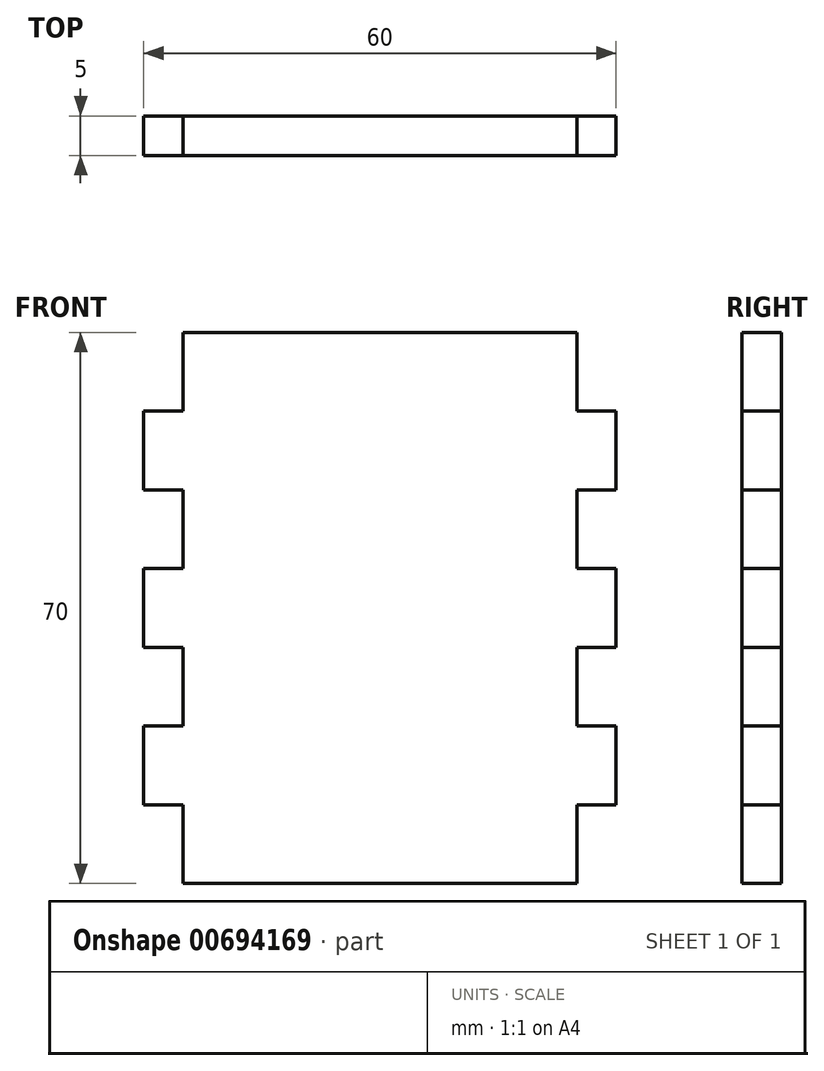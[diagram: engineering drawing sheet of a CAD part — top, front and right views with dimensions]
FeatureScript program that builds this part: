
annotation { "Feature Type Name" : "Feature", "Feature Type Description" : "" }
export const myFeature = defineFeature(function(context is Context, id is Id, definition is map)
    precondition{}
    {
        {
            var Q0;
            Q0=qCreatedBy(makeId("Front.planeOp"),FACE);
            var sketch = newSketch(context, id + "F0", { "sketchPlane" : qUnion([Q0])});
            skLineSegment(sketch, "E0.bottom", {"start": v(0, 70) * mm, "end": v(-25, 70) * mm});
            skLineSegment(sketch, "E0.top", {"start": v(0, 0) * mm, "end": v(-25, 0) * mm});
            skLineSegment(sketch, "E0.left", {"start": v(0, 70) * mm, "end": v(0, 0) * mm});
            skLineSegment(sketch, "E0.right", {"start": v(-30, 60) * mm, "end": v(-30, 50) * mm});
            skLineSegment(sketch, "E1.top", {"start": v(-30, 60) * mm, "end": v(-25, 60) * mm});
            skLineSegment(sketch, "E1.right", {"start": v(-25, 70) * mm, "end": v(-25, 60) * mm});
            skLineSegment(sketch, "E2.bottom", {"start": v(-30, 50) * mm, "end": v(-25, 50) * mm});
            skLineSegment(sketch, "E2.top", {"start": v(-30, 40) * mm, "end": v(-25, 40) * mm});
            skLineSegment(sketch, "E2.right", {"start": v(-25, 50) * mm, "end": v(-25, 40) * mm});
            skLineSegment(sketch, "E3.bottom", {"start": v(-30, 30) * mm, "end": v(-25, 30) * mm});
            skLineSegment(sketch, "E3.top", {"start": v(-30, 20) * mm, "end": v(-25, 20) * mm});
            skLineSegment(sketch, "E3.right", {"start": v(-25, 30) * mm, "end": v(-25, 20) * mm});
            skLineSegment(sketch, "E4.bottom", {"start": v(-30, 10) * mm, "end": v(-25, 10) * mm});
            skLineSegment(sketch, "E4.right", {"start": v(-25, 10) * mm, "end": v(-25, 0) * mm});
            skLineSegment(sketch, "E5.trimOffspring", {"start": v(-30, 40) * mm, "end": v(-30, 30) * mm});
            skLineSegment(sketch, "E6.trimOffspring", {"start": v(-30, 20) * mm, "end": v(-30, 10) * mm});
            skLineSegment(sketch, "E7.MirrorCS", {"start": v(25, 10) * mm, "end": v(25, 0) * mm});
            skLineSegment(sketch, "E8.MirrorCS", {"start": v(30, 40) * mm, "end": v(30, 30) * mm});
            skLineSegment(sketch, "E9.MirrorCS", {"start": v(30, 20) * mm, "end": v(30, 10) * mm});
            skLineSegment(sketch, "E10.MirrorCS", {"start": v(0, 70) * mm, "end": v(25, 70) * mm});
            skLineSegment(sketch, "E11.MirrorCS", {"start": v(0, 0) * mm, "end": v(25, 0) * mm});
            skLineSegment(sketch, "E12.MirrorCS", {"start": v(30, 10) * mm, "end": v(25, 10) * mm});
            skLineSegment(sketch, "E13.MirrorCS", {"start": v(25, 30) * mm, "end": v(25, 20) * mm});
            skLineSegment(sketch, "E14.MirrorCS", {"start": v(30, 20) * mm, "end": v(25, 20) * mm});
            skLineSegment(sketch, "E15.MirrorCS", {"start": v(30, 60) * mm, "end": v(30, 50) * mm});
            skLineSegment(sketch, "E16.MirrorCS", {"start": v(30, 60) * mm, "end": v(25, 60) * mm});
            skLineSegment(sketch, "E17.MirrorCS", {"start": v(25, 70) * mm, "end": v(25, 60) * mm});
            skLineSegment(sketch, "E18.MirrorCS", {"start": v(30, 30) * mm, "end": v(25, 30) * mm});
            skLineSegment(sketch, "E19.MirrorCS", {"start": v(25, 50) * mm, "end": v(25, 40) * mm});
            skLineSegment(sketch, "E20.MirrorCS", {"start": v(30, 40) * mm, "end": v(25, 40) * mm});
            skLineSegment(sketch, "E21.MirrorCS", {"start": v(30, 50) * mm, "end": v(25, 50) * mm});
            skSolve(sketch);
        }
        {
            var Q0;
            Q0=qSketchRegion(id+"F0",true);
            extrude(context, id + "F1", {"entities" : qUnion([Q0]), "depth" : 5 * mm, "offsetDistance" : 25 * mm});
        }
    });
